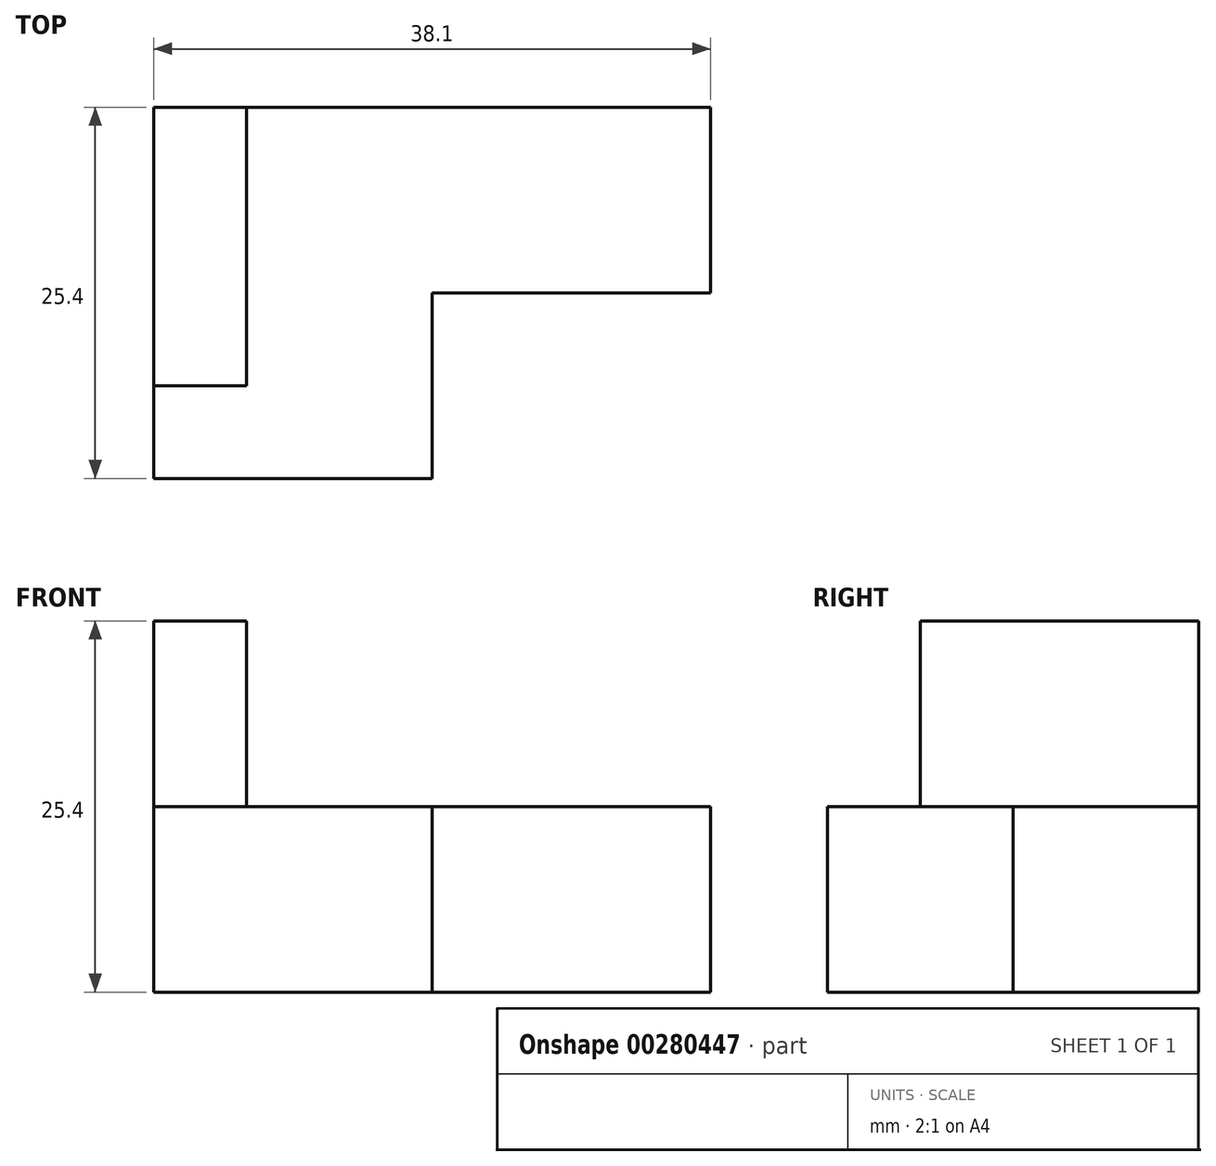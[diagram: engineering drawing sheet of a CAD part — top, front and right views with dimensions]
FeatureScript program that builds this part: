
annotation { "Feature Type Name" : "Feature", "Feature Type Description" : "" }
export const myFeature = defineFeature(function(context is Context, id is Id, definition is map)
    precondition{}
    {
        {
            var Q0;
            Q0=qCreatedBy(makeId("Top.planeOp"),FACE);
            var sketch = newSketch(context, id + "F0", { "sketchPlane" : qUnion([Q0])});
            skLineSegment(sketch, "E0", {"start": v(0, 0) * mm, "end": v(0, 25.4) * mm});
            skLineSegment(sketch, "E1", {"start": v(0, 25.4) * mm, "end": v(38.1, 25.4) * mm});
            skLineSegment(sketch, "E2", {"start": v(38.1, 25.4) * mm, "end": v(38.1, 0) * mm});
            skLineSegment(sketch, "E3", {"start": v(38.1, 0) * mm, "end": v(0, 0) * mm});
            skSolve(sketch);
        }
        {
            var Q0;
            Q0 = qSketchRegion(id + "F0", true);
            extrude(context, id + "F1", {"entities" : qUnion([Q0]), "depth" : 12.7 * mm});
        }
        {
            var Q0;
            Q0=makeQuery(id+"F1.opExtrude","CAP_FACE",FACE,{"disambiguationData":[OSD([sQuery(id+"F0.wireOp",EDGE,"E0"),sQuery(id+"F0.wireOp",EDGE,"E1"),sQuery(id+"F0.wireOp",EDGE,"E2"),sQuery(id+"F0.wireOp",EDGE,"E3")])],"isStart":false});
            var sketch = newSketch(context, id + "F2", { "sketchPlane" : qUnion([Q0])});
            skLineSegment(sketch, "E4.bottom", {"start": v(38.1, 0) * mm, "end": v(19.05, 0) * mm});
            skLineSegment(sketch, "E4.top", {"start": v(38.1, 12.7) * mm, "end": v(19.05, 12.7) * mm});
            skLineSegment(sketch, "E4.left", {"start": v(38.1, 0) * mm, "end": v(38.1, 12.7) * mm});
            skLineSegment(sketch, "E4.right", {"start": v(19.05, 0) * mm, "end": v(19.05, 12.7) * mm});
            skSolve(sketch);
        }
        {
            var Q0;
            Q0 = qSketchRegion(id + "F2", true);
            extrude(context, id + "F3", {"entities" : qUnion([Q0]), "operationType" : NewBodyOperationType.REMOVE, "endBound" : BoundingType.THROUGH_ALL, "oppositeDirection" : true, "depth" : 25.4 * mm});
        }
        {
            var Q0;
            Q0=makeQuery(id+"F1.opExtrude","CAP_FACE",FACE,{"disambiguationData":[OSD([sQuery(id+"F0.wireOp",EDGE,"E0"),sQuery(id+"F0.wireOp",EDGE,"E1"),sQuery(id+"F0.wireOp",EDGE,"E2"),sQuery(id+"F0.wireOp",EDGE,"E3")])],"isStart":false});
            var sketch = newSketch(context, id + "F4", { "sketchPlane" : qUnion([Q0])});
            skLineSegment(sketch, "E5.bottom", {"start": v(0, 25.4) * mm, "end": v(6.35, 25.4) * mm});
            skLineSegment(sketch, "E5.top", {"start": v(0, 6.35) * mm, "end": v(6.35, 6.35) * mm});
            skLineSegment(sketch, "E5.left", {"start": v(0, 25.4) * mm, "end": v(0, 6.35) * mm});
            skLineSegment(sketch, "E5.right", {"start": v(6.35, 25.4) * mm, "end": v(6.35, 6.35) * mm});
            skSolve(sketch);
        }
        {
            var Q0;
            Q0 = qSketchRegion(id + "F4", true);
            extrude(context, id + "F5", {"entities" : qUnion([Q0]), "operationType" : NewBodyOperationType.ADD, "depth" : 12.7 * mm});
        }
    });
